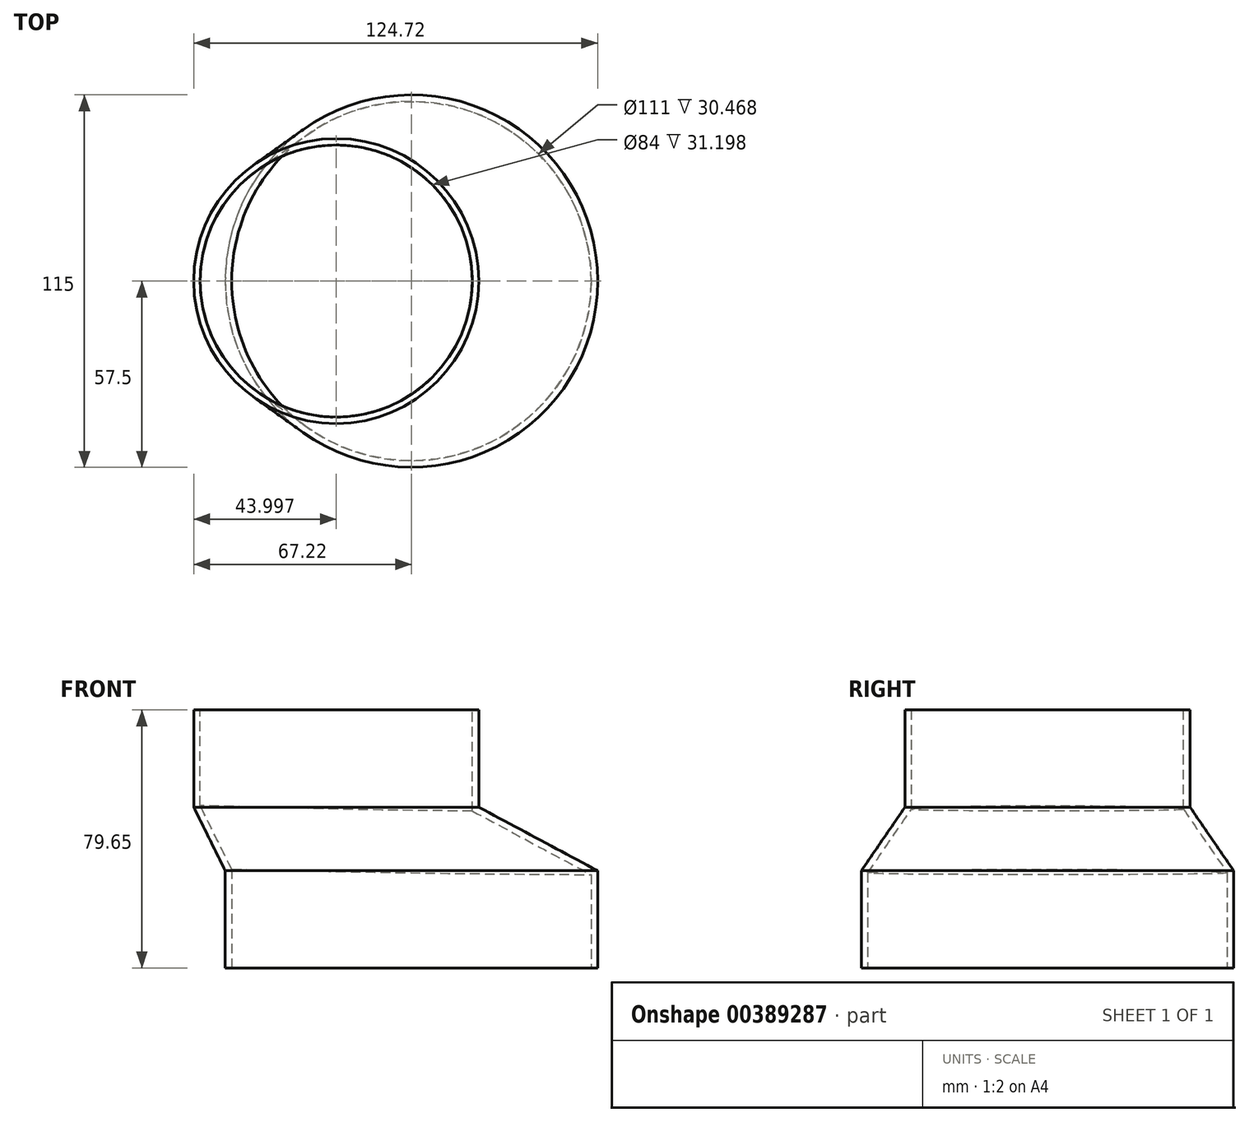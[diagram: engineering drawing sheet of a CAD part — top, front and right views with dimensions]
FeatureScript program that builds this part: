
annotation { "Feature Type Name" : "Feature", "Feature Type Description" : "" }
export const myFeature = defineFeature(function(context is Context, id is Id, definition is map)
    precondition{}
    {
        {
            var Q0;
            Q0=qCreatedBy(makeId("Front.planeOp"),FACE);
            var sketch = newSketch(context, id + "F0", { "sketchPlane" : qUnion([Q0])});
            skLineSegment(sketch, "E0.bottom", {"start": v(0, 0) * mm, "end": v(-57.5, 0) * mm});
            skLineSegment(sketch, "E0.top", {"start": v(0, 30) * mm, "end": v(-57.5, 30) * mm});
            skLineSegment(sketch, "E0.left", {"start": v(0, 0) * mm, "end": v(0, 30) * mm});
            skLineSegment(sketch, "E0.right", {"start": v(-57.5, 0) * mm, "end": v(-57.5, 30) * mm});
            skLineSegment(sketch, "E1.bottom", {"start": v(-63.28, 71.65) * mm, "end": v(-19.28, 71.65) * mm});
            skLineSegment(sketch, "E1.top", {"start": v(-63.28, 41.65) * mm, "end": v(-19.28, 41.65) * mm});
            skLineSegment(sketch, "E1.left", {"start": v(-63.28, 71.65) * mm, "end": v(-63.28, 41.65) * mm});
            skLineSegment(sketch, "E1.right", {"start": v(-19.28, 71.65) * mm, "end": v(-19.28, 41.65) * mm});
            skSolve(sketch);
        }
        {
            var Q0;
            Q0=makeQuery(id+"F0.imprint","IMPRINT",FACE,{"disambiguationData":[TD([[makeQuery(id+"F0.imprint","IMPRINT",EDGE,{"derivedFrom":sQuery(id+"F0.wireOp",EDGE,"E0.bottom")}),-1.0]])]});
            var Q1;
            Q1=sQuery(id+"F0.wireOp",EDGE,"E0.left");
            revolve(context, id + "F1", {"surfaceOperationType" : NewSurfaceOperationType.NEW, "entities" : qUnion([Q0]), "axis" : qUnion([Q1]), "revolveType" : RevolveType.FULL});
        }
        {
            var Q0;
            Q0=qCreatedBy(makeId("Front.planeOp"),FACE);
            var sketch = newSketch(context, id + "F2", { "sketchPlane" : qUnion([Q0])});
            skLineSegment(sketch, "E2.bottom", {"start": v(-67.22, 79.65) * mm, "end": v(-23.22, 79.65) * mm});
            skLineSegment(sketch, "E2.top", {"start": v(-67.22, 49.65) * mm, "end": v(-23.22, 49.65) * mm});
            skLineSegment(sketch, "E2.left", {"start": v(-67.22, 79.65) * mm, "end": v(-67.22, 49.65) * mm});
            skLineSegment(sketch, "E2.right", {"start": v(-23.22, 79.65) * mm, "end": v(-23.22, 49.65) * mm});
            skSolve(sketch);
        }
        {
            var Q0;
            Q0=makeQuery(id+"F2.imprint","IMPRINT",FACE,{"disambiguationData":[TD([[makeQuery(id+"F2.imprint","IMPRINT",EDGE,{"derivedFrom":sQuery(id+"F2.wireOp",EDGE,"E2.bottom")}),-1.0]])]});
            var Q1;
            Q1 = qConstructionFilter(qBodyType(qCreatedBy(id + "F2" ,EDGE), BodyType.WIRE), ConstructionObject.NO);
            var Q2;
            Q2=sQuery(id+"F2.wireOp",EDGE,"E2.right");
            revolve(context, id + "F3", {"surfaceOperationType" : NewSurfaceOperationType.NEW, "entities" : qUnion([Q0]), "surfaceEntities" : qUnion([Q1]), "axis" : qUnion([Q2]), "revolveType" : RevolveType.FULL});
        }
        {
            var Q0;
            Q0=makeQuery(id+"F3.opRevolve","SWEPT_FACE",FACE,{"disambiguationData":[OSD([sQuery(id+"F2.wireOp",EDGE,"E2.top")])]});
            var Q1;
            Q1=makeQuery(id+"F1.opRevolve","SWEPT_FACE",FACE,{"disambiguationData":[OSD([sQuery(id+"F0.wireOp",EDGE,"E0.top")])]});
            loft(context, id + "F4", {"operationType" : NewBodyOperationType.ADD, "sheetProfilesArray" : [{ "sheetProfileEntities" : qUnion([Q0]) }, { "sheetProfileEntities" : qUnion([Q1]) }]});
        }
        {
            var Q0;
            Q0=makeQuery(id+"F3.opRevolve","SWEPT_FACE",FACE,{"disambiguationData":[OSD([sQuery(id+"F2.wireOp",EDGE,"E2.bottom")])]});
            var Q1;
            Q1=makeQuery(id+"F1.opRevolve","SWEPT_FACE",FACE,{"disambiguationData":[OSD([sQuery(id+"F0.wireOp",EDGE,"E0.bottom")])]});
            shell(context, id + "F5", {"entities" : qUnion([Q0, Q1]), "thickness" : 2 * mm});
        }
    });
